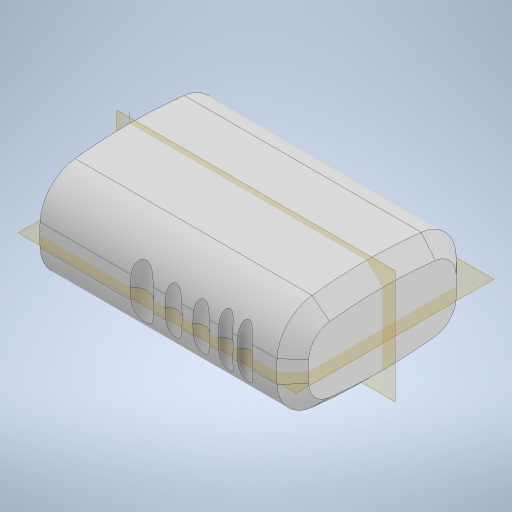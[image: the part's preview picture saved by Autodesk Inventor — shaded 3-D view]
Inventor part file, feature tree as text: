
AUTODESK INVENTOR PART (.ipt)
format: ipt  version: 2023 (Build 270158030, 158C)  size: 434,176 bytes
history: native  units: mm
features: extrude x3, sketch x3, fillet x2, chamfer x2, mirror x1, projected_geometry x1
ambient origin geometry x8: Origin, YZ Plane, XZ Plane, XY Plane, X Axis, Y Axis, Z Axis, Center Point
bodies: Solid1 (feature_tree)
feature tree (12):
  extrude  "Extrusion1"  Depth=30.0mm
  extrude  "Extrusion2"  Depth=30.0mm
  fillet  "Fillet1"  Radius=9.4mm
  chamfer  "Chamfer1"  Distance=1.0mm
  fillet  "Fillet3"  Radius=30.0mm
  chamfer  "Chamfer2"  Distance=2.0mm
  extrude  "Extrusion3"  Depth=10.0mm
  mirror  "Mirror1"
  sketch  "Sketch1"  dims[d0=60.0mm d1=30.0mm]
  sketch  "Sketch2"  dims[d2=60.0mm d3=30.0mm d4=9.4mm]
  projected_geometry  "Projected Loop1"
  sketch  "Sketch3"  dims[d5=20.0mm d6=1.0mm d7=30.0mm d8=0.0mm d9=2.0mm d10=0.0mm d11=5.0mm d13=2.0mm d14=2.0mm d15=45.0deg d16=3.0mm d17=1.0mm d18=2.0mm d19=45.0deg d20=4.7mm d21=10.0mm d22=3.0mm d23=2.0mm d24=2.0mm d25=2.0mm d26=-0.349066mm d27=3.0mm d28=4.0mm]
